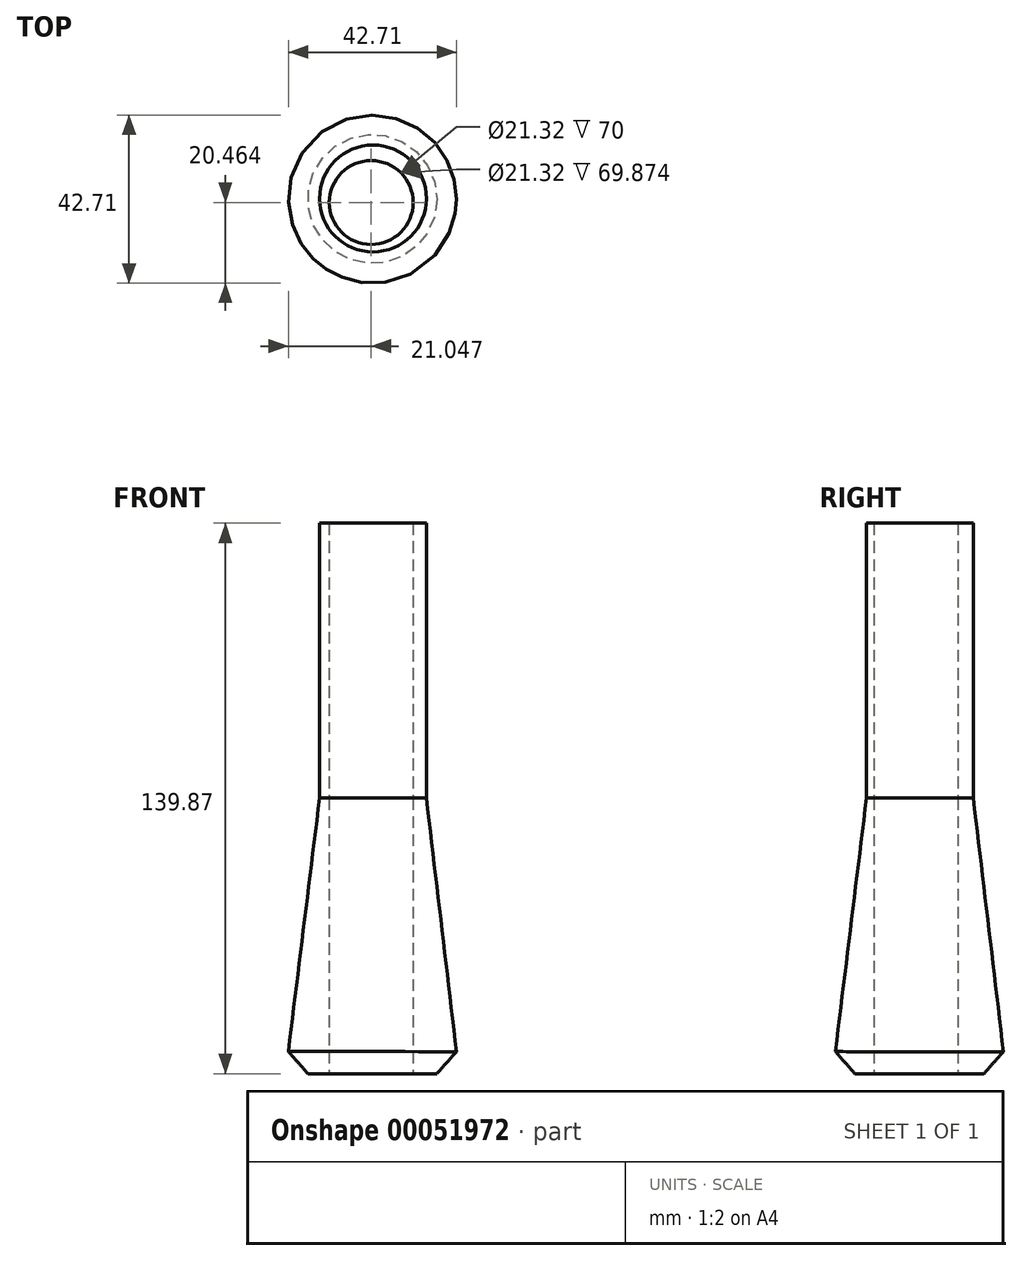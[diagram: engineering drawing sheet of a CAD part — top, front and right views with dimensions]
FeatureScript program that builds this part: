
annotation { "Feature Type Name" : "Feature", "Feature Type Description" : "" }
export const myFeature = defineFeature(function(context is Context, id is Id, definition is map)
    precondition{}
    {
        {
            var Q0;
            Q0=qCreatedBy(makeId("Top.planeOp"),FACE);
            var sketch = newSketch(context, id + "F0", { "sketchPlane" : qUnion([Q0])});
            skCircle(sketch, "E0", {"center": v(-32.68, 44.57) * mm, "radius": 13.57 * mm});
            skSolve(sketch);
        }
        {
            var Q0;
            Q0 = qSketchRegion(id + "F0", true);
            extrude(context, id + "F1", {"entities" : qUnion([Q0]), "depth" : 69.87 * mm});
        }
        {
            var Q0;
            Q0=qCreatedBy(makeId("Top.planeOp"),FACE);
            cPlane(context, id + "F2", {"entities" : qUnion([Q0]), "cplaneType" : CPlaneType.OFFSET, "offset" : 70 * mm, "oppositeDirection" : true, "width" : 150 * mm, "height" : 150 * mm});
        }
        {
            var Q0;
            Q0=qCreatedBy(id+"F2.planeOp",FACE);
            var sketch = newSketch(context, id + "F3", { "sketchPlane" : qUnion([Q0])});
            skCircle(sketch, "E1", {"center": v(-32.85, 44.43) * mm, "radius": 22.03 * mm});
            skSolve(sketch);
        }
        {
            var Q0;
            Q0=makeQuery(id+"F3.imprint","IMPRINT",FACE,{"disambiguationData":[TD([[makeQuery(id+"F3.imprint","IMPRINT",EDGE,{"derivedFrom":sQuery(id+"F3.wireOp",EDGE,"E1")}),1.0]])]});
            var Q1;
            Q1=makeQuery(id+"F1.opExtrude","CAP_FACE",FACE,{"disambiguationData":[OSD([sQuery(id+"F0.wireOp",EDGE,"E0")])],"isStart":true});
            loft(context, id + "F4", {"sheetProfilesArray" : [{ "sheetProfileEntities" : qUnion([Q0]) }, { "sheetProfileEntities" : qUnion([Q1]) }]});
        }
        {
            var Q0;
            Q0=qCreatedBy(id+"F2.planeOp",FACE);
            var sketch = newSketch(context, id + "F5", { "sketchPlane" : qUnion([Q0])});
            skCircle(sketch, "E2", {"center": v(-33.14, 43.55) * mm, "radius": 10.66 * mm});
            skSolve(sketch);
        }
        {
            var Q0;
            Q0 = qSketchRegion(id + "F5", true);
            extrude(context, id + "F6", {"entities" : qUnion([Q0]), "operationType" : NewBodyOperationType.REMOVE, "depth" : 146.08 * mm});
        }
        {
            var Q0;
            Q0=makeQuery(id+"F4.opLoft","MID_CAP_EDGE",EDGE,{"disambiguationData":[OSD([sQuery(id+"F3.wireOp",EDGE,"E1")])],"capPos":0.0});
            chamfer(context, id + "F7", {"entities" : qUnion([Q0]), "width" : 5 * mm, "tangentPropagation" : true});
        }
        {
            var Q0;
            Q0=qCreatedBy(makeId("Top.planeOp"),FACE);
            var sketch = newSketch(context, id + "F8", { "sketchPlane" : qUnion([Q0])});
            skCircle(sketch, "E3", {"center": v(-32.7, 44.98) * mm, "radius": 8.36 * mm});
            skSolve(sketch);
        }
        {
            var Q0;
            Q0=makeQuery(id+"F8.imprint","IMPRINT",FACE,{"disambiguationData":[TD([[makeQuery(id+"F8.imprint","IMPRINT",EDGE,{"derivedFrom":sQuery(id+"F8.wireOp",EDGE,"E3")}),1.0]])]});
            extrude(context, id + "F9", {"entities" : qUnion([Q0]), "operationType" : NewBodyOperationType.REMOVE, "depth" : 78.02 * mm});
        }
    });
